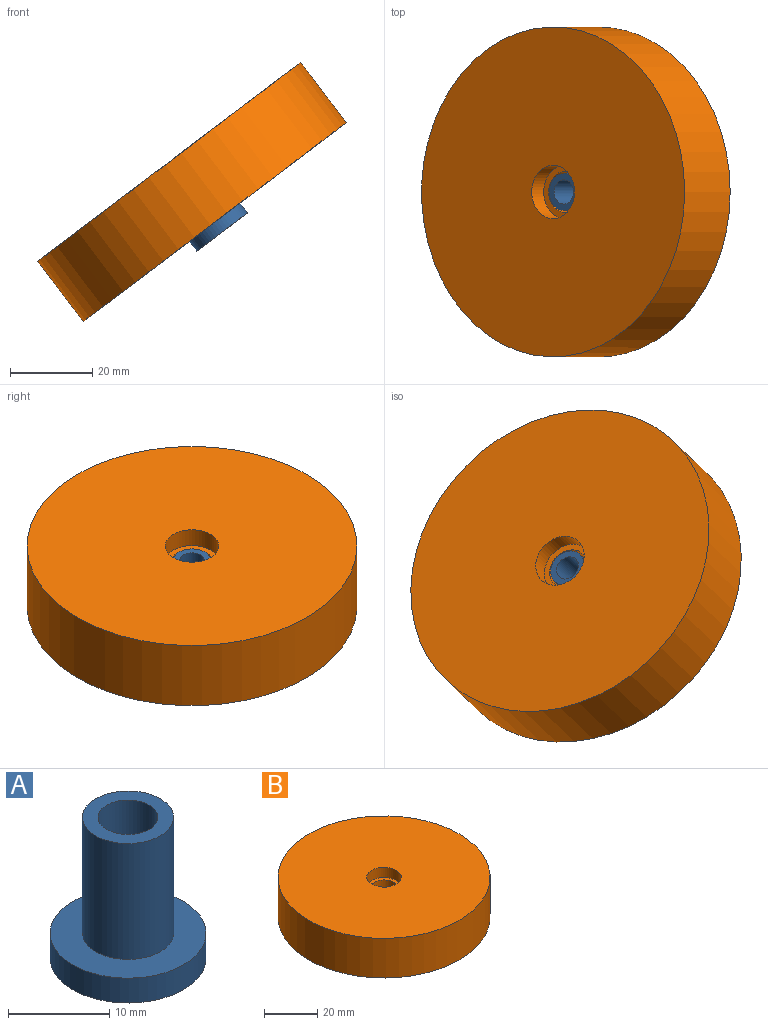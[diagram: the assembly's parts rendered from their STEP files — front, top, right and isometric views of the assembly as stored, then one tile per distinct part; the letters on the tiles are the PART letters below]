
ASSEMBLY  parts=2 mates=1
PART A: 6 faces, bbox 15.4x15.4x17 mm
  f0: cylinder r=2.95mm len=17mm, axis (0,0,-1), area 315.1mm2, adj f3,f5
  f1: cylinder r=7.7mm len=15.4mm, axis (0,0,-1), area 145.1mm2, adj f2,f3
  f2: plane 15.4x15.4mm, normal (0,0,1), area 122.6mm2, adj f1,f4
  f3: plane 15.4x15.4mm, normal (0,0,-1), area 158.9mm2, adj f0,f1
  f4: cylinder r=4.5mm len=14mm, axis (0,0,-1), area 395.8mm2, adj f2,f5
  f5: plane 9x9mm, normal (0,0,1), area 36.3mm2, adj f0,f4
PART B: 6 faces, bbox 80x80x18.3 mm
  f0: cylinder r=5mm len=13.5mm, axis (0,0,-1), area 424.1mm2, adj f3,f5
  f1: cylinder r=40mm len=80mm, axis (0,0,-1), area 4599.3mm2, adj f2,f3
  f2: plane 80x80mm, normal (0,0,1), area 4893.8mm2, adj f1,f4
  f3: plane 80x80mm, normal (0,0,-1), area 4948mm2, adj f0,f1
  f4: cylinder r=6.5mm len=13mm, axis (0,0,1), area 196mm2, adj f2,f5
  f5: plane 13x13mm, normal (0,0,1), area 54.2mm2, adj f0,f4
PLACE A rot(axis=(0,-1,0),37.1deg) t=(-5.49,0.38,-0.19)mm
PLACE B rot(axis=(0,-1,0),37.1deg) t=(-7.3,0.38,2.2)mm
MATE revolute A.f4 <-> B.f0  axis (-0.6,0,0.8) through (-7.3,0.38,2.2)mm
